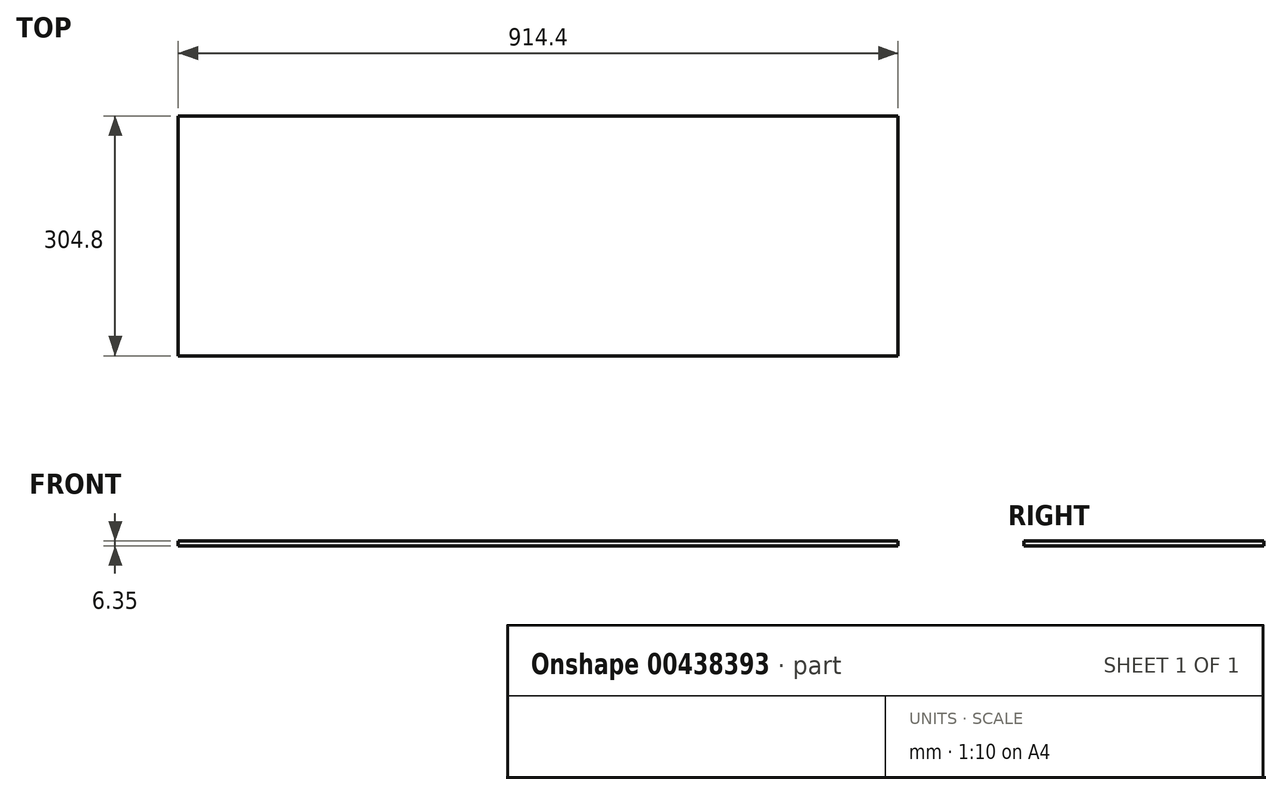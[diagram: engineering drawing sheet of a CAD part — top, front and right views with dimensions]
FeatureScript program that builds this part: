
annotation { "Feature Type Name" : "Feature", "Feature Type Description" : "" }
export const myFeature = defineFeature(function(context is Context, id is Id, definition is map)
    precondition{}
    {
        {
            var Q0;
            Q0=qCreatedBy(makeId("Front.planeOp"),FACE);
            var sketch = newSketch(context, id + "F0", { "sketchPlane" : qUnion([Q0])});
            skLineSegment(sketch, "E0.bottom", {"start": v(-819.96, 16.11) * mm, "end": v(94.44, 16.11) * mm});
            skLineSegment(sketch, "E0.top", {"start": v(-819.96, 9.76) * mm, "end": v(94.44, 9.76) * mm});
            skLineSegment(sketch, "E0.left", {"start": v(-819.96, 16.11) * mm, "end": v(-819.96, 9.76) * mm});
            skLineSegment(sketch, "E0.right", {"start": v(94.44, 16.11) * mm, "end": v(94.44, 9.76) * mm});
            skSolve(sketch);
        }
        {
            var Q0;
            Q0=makeQuery(id+"F0.imprint","IMPRINT",FACE,{"disambiguationData":[TD([[makeQuery(id+"F0.imprint","IMPRINT",EDGE,{"derivedFrom":sQuery(id+"F0.wireOp",EDGE,"E0.bottom")}),-1.0]])]});
            extrude(context, id + "F1", {"entities" : qUnion([Q0]), "depth" : 304.8 * mm});
        }
    });
